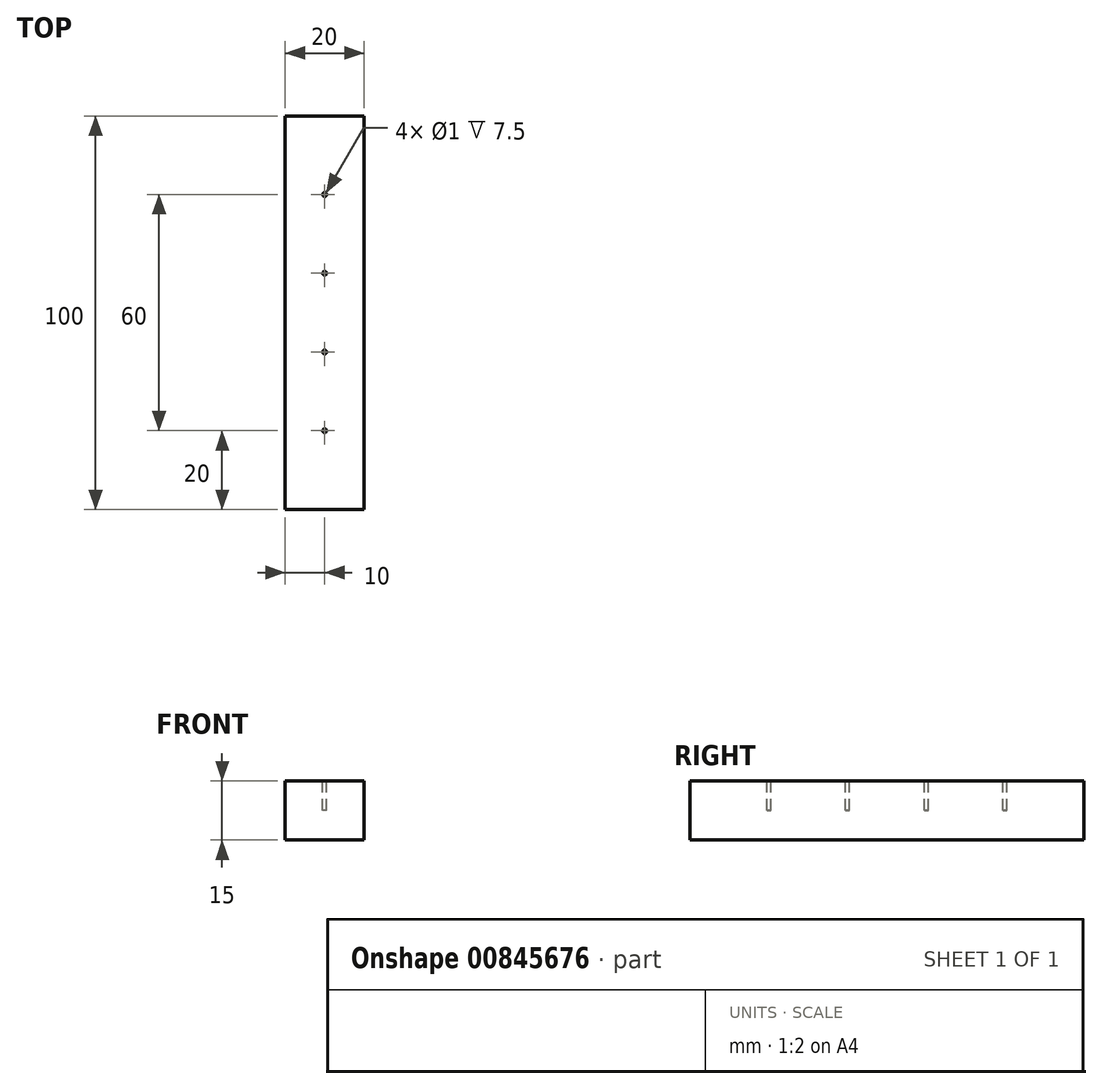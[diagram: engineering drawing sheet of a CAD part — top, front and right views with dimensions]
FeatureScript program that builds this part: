
annotation { "Feature Type Name" : "Feature", "Feature Type Description" : "" }
export const myFeature = defineFeature(function(context is Context, id is Id, definition is map)
    precondition{}
    {
        {
            var Q0;
            Q0=qCreatedBy(makeId("Front.planeOp"),FACE);
            var sketch = newSketch(context, id + "F0", { "sketchPlane" : qUnion([Q0])});
            skLineSegment(sketch, "E0.bottom", {"start": v(0, 0) * mm, "end": v(20, 0) * mm});
            skLineSegment(sketch, "E0.top", {"start": v(0, 15) * mm, "end": v(20, 15) * mm});
            skLineSegment(sketch, "E0.left", {"start": v(0, 0) * mm, "end": v(0, 15) * mm});
            skLineSegment(sketch, "E0.right", {"start": v(20, 0) * mm, "end": v(20, 15) * mm});
            skSolve(sketch);
        }
        {
            var Q0;
            Q0=makeQuery(id+"F0.imprint","IMPRINT",FACE,{"disambiguationData":[TD([[makeQuery(id+"F0.imprint","IMPRINT",EDGE,{"derivedFrom":sQuery(id+"F0.wireOp",EDGE,"E0.bottom")}),1.0]])]});
            extrude(context, id + "F1", {"entities" : qUnion([Q0]), "depth" : 100 * mm, "offsetDistance" : 25 * mm});
        }
        {
            var Q0;
            Q0=makeQuery(id+"F1.opExtrude","SWEPT_FACE",FACE,{"disambiguationData":[OSD([sQuery(id+"F0.wireOp",EDGE,"E0.top")])]});
            var sketch = newSketch(context, id + "F2", { "sketchPlane" : qUnion([Q0])});
            skCircle(sketch, "E1", {"center": v(10, -80) * mm, "radius": 0.5 * mm});
            skCircle(sketch, "E2", {"center": v(10, -60) * mm, "radius": 0.5 * mm});
            skCircle(sketch, "E3", {"center": v(10, -40) * mm, "radius": 0.5 * mm});
            skCircle(sketch, "E4", {"center": v(10, -20) * mm, "radius": 0.5 * mm});
            skSolve(sketch);
        }
        {
            var Q0;
            Q0 = qSketchRegion(id + "F2", true);
            extrude(context, id + "F3", {"entities" : qUnion([Q0]), "operationType" : NewBodyOperationType.REMOVE, "oppositeDirection" : true, "depth" : 7.5 * mm, "offsetDistance" : 25 * mm});
        }
    });
